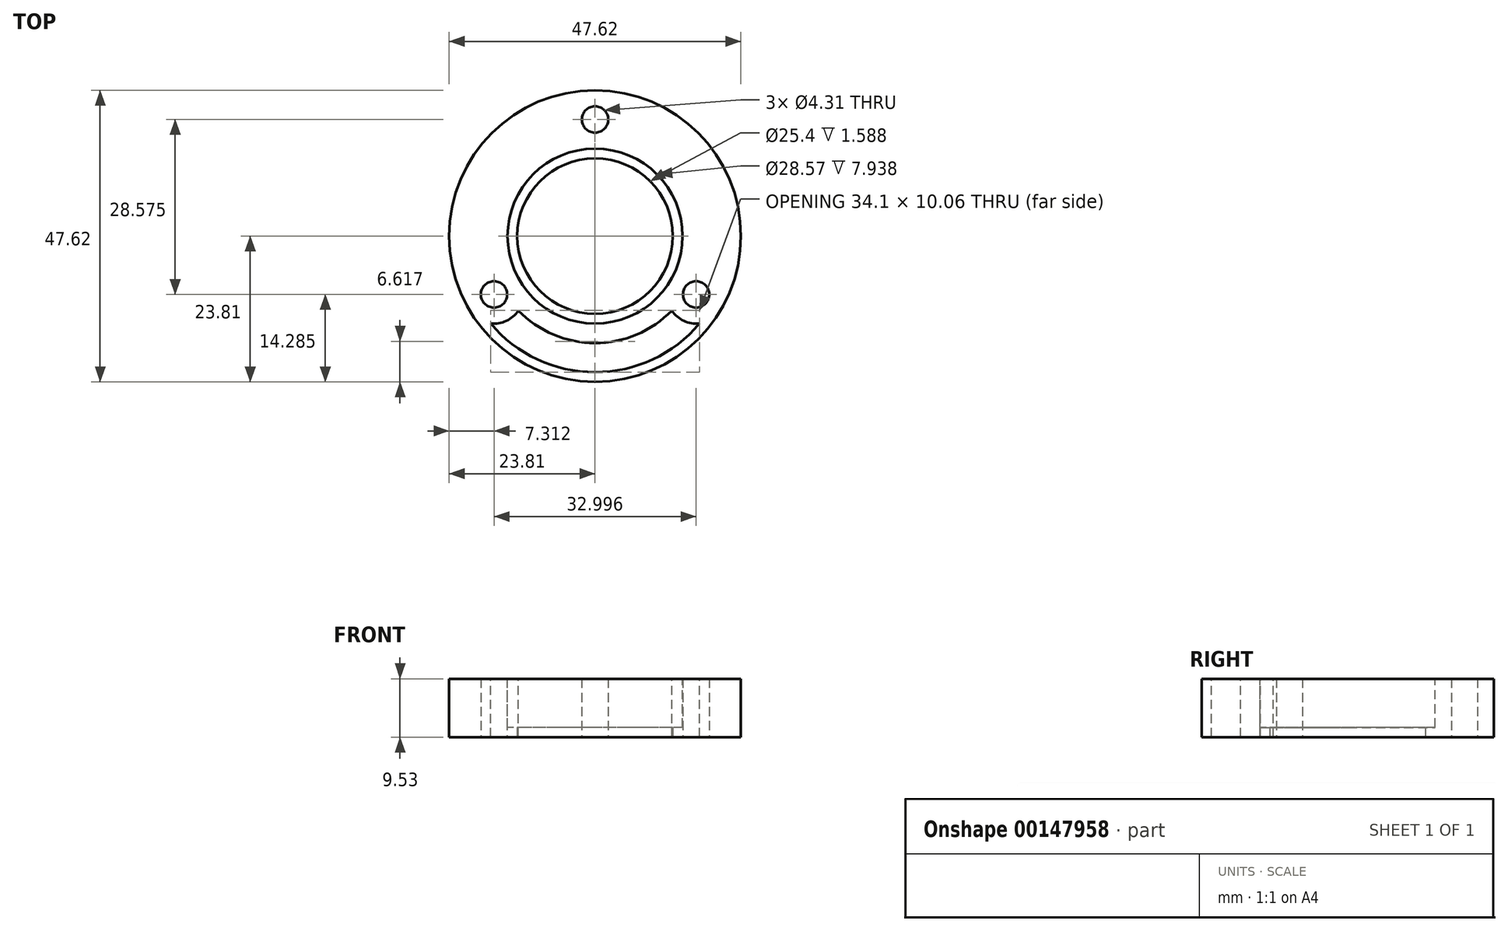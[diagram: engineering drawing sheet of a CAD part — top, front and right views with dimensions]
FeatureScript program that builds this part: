
annotation { "Feature Type Name" : "Feature", "Feature Type Description" : "" }
export const myFeature = defineFeature(function(context is Context, id is Id, definition is map)
    precondition{}
    {
        {
            var Q0;
            Q0=qCreatedBy(makeId("Top.planeOp"),FACE);
            var sketch = newSketch(context, id + "F0", { "sketchPlane" : qUnion([Q0])});
            skCircle(sketch, "E0", {"center": v(0, 0) * mm, "radius": 12.7 * mm});
            skCircle(sketch, "E1", {"center": v(0, 0) * mm, "radius": 14.29 * mm, "construction": true});
            skCircle(sketch, "E2", {"center": v(0, 0) * mm, "radius": 23.81 * mm});
            skCircle(sketch, "E3", {"center": v(0, 19.05) * mm, "radius": 4.76 * mm, "construction": true});
            skCircle(sketch, "E4.cCircle", {"center": v(0, 0) * mm, "radius": 9.53 * mm, "construction": true});
            skLineSegment(sketch, "E4.0", {"start": v(16.5, -9.53) * mm, "end": v(-16.5, -9.53) * mm, "construction": true});
            skLineSegment(sketch, "E4.1", {"start": v(-16.5, -9.53) * mm, "end": v(0, 19.05) * mm, "construction": true});
            skLineSegment(sketch, "E4.2", {"start": v(0, 19.05) * mm, "end": v(16.5, -9.52) * mm, "construction": true});
            skPoint(sketch, "E4.0.midPoint", {"position": v(0, -9.53) * mm});
            skCircle(sketch, "E5", {"center": v(0, 19.05) * mm, "radius": 2.15 * mm});
            skCircle(sketch, "E6", {"center": v(16.5, -9.53) * mm, "radius": 2.15 * mm});
            skCircle(sketch, "E7", {"center": v(-16.5, -9.53) * mm, "radius": 2.15 * mm});
            skSolve(sketch);
        }
        {
            var Q0;
            Q0=qSketchRegion(id+"F0",true);
            extrude(context, id + "F1", {"entities" : qUnion([Q0]), "depth" : 9.52 * mm});
        }
        {
            var Q0;
            Q0=makeQuery(id+"F1.opExtrude","CAP_FACE",FACE,{"disambiguationData":[OSD([sQuery(id+"F0.wireOp",EDGE,"E0"),sQuery(id+"F0.wireOp",EDGE,"E2"),sQuery(id+"F0.wireOp",EDGE,"E5"),sQuery(id+"F0.wireOp",EDGE,"E6"),sQuery(id+"F0.wireOp",EDGE,"E7")])],"isStart":false});
            var sketch = newSketch(context, id + "F2", { "sketchPlane" : qUnion([Q0])});
            skCircle(sketch, "E8", {"center": v(0, 0) * mm, "radius": 14.29 * mm});
            skSolve(sketch);
        }
        {
            var Q0;
            Q0=qSketchRegion(id+"F2",true);
            extrude(context, id + "F3", {"entities" : qUnion([Q0]), "operationType" : NewBodyOperationType.REMOVE, "oppositeDirection" : true, "depth" : 7.94 * mm});
        }
        {
            var Q0;
            Q0=makeQuery(id+"F1.opExtrude","CAP_FACE",FACE,{"disambiguationData":[OSD([sQuery(id+"F0.wireOp",EDGE,"E0"),sQuery(id+"F0.wireOp",EDGE,"E2"),sQuery(id+"F0.wireOp",EDGE,"E5"),sQuery(id+"F0.wireOp",EDGE,"E6"),sQuery(id+"F0.wireOp",EDGE,"E7")])],"isStart":false});
            var sketch = newSketch(context, id + "F4", { "sketchPlane" : qUnion([Q0])});
            skArc(sketch, "E9", {"start": v(12.53, -12.16) * mm, "mid": v(14.5, -13.85) * mm, "end": v(17.05, -14.26) * mm});
            skArc(sketch, "E10", {"start": v(-17.05, -14.26) * mm, "mid": v(-14.5, -13.85) * mm, "end": v(-12.53, -12.16) * mm});
            skArc(sketch, "E11", {"start": v(-17.05, -14.26) * mm, "mid": v(0, -22.23) * mm, "end": v(17.05, -14.26) * mm});
            skArc(sketch, "E12", {"start": v(-12.53, -12.16) * mm, "mid": v(0, -17.46) * mm, "end": v(12.53, -12.16) * mm});
            skSolve(sketch);
        }
        {
            var Q0;
            Q0=qSketchRegion(id+"F4",true);
            var Q1;
            Q1=makeQuery(id+"F1.opExtrude","CAP_FACE",FACE,{"disambiguationData":[OSD([sQuery(id+"F0.wireOp",EDGE,"E0"),sQuery(id+"F0.wireOp",EDGE,"E2"),sQuery(id+"F0.wireOp",EDGE,"E5"),sQuery(id+"F0.wireOp",EDGE,"E6"),sQuery(id+"F0.wireOp",EDGE,"E7")])],"isStart":true});
            extrude(context, id + "F5", {"entities" : qUnion([Q0]), "operationType" : NewBodyOperationType.REMOVE, "endBound" : BoundingType.UP_TO_SURFACE, "oppositeDirection" : true, "endBoundEntityFace" : qUnion([Q1]), "depth" : 25.4 * mm});
        }
    });
